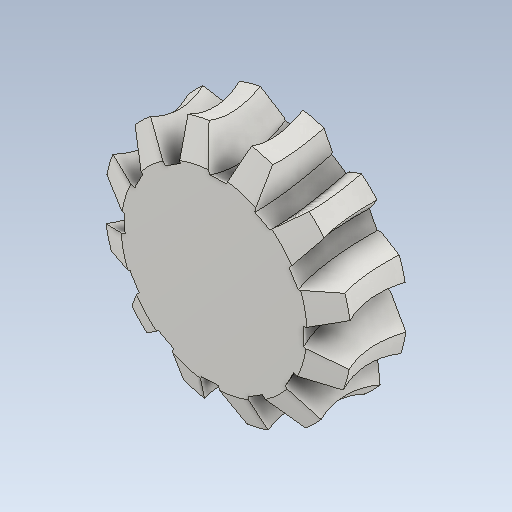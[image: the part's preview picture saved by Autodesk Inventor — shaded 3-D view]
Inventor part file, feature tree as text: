
AUTODESK INVENTOR PART (.ipt)
format: ipt  version: 2021 (Build 250183000, 183)  size: 324,096 bytes
history: native  units: mm (DEFAULTED — no unit token found)
features: other x8, plane x3, pattern_circular x1, sketch x1
ambient origin geometry x5: Origin, X Axis, Y Axis, Z Axis, Center Point
bodies: Solid1 (feature_tree)
feature tree (13):
  other  "Tooth Plane"
  other  "Base Body Sketch"
  other  "Base Body"
  other  "Base Body2"
  plane  "Work Plane13"
  other  "Tooth"
  pattern_circular  "Tooth Pattern"  [2 undecoded]
  plane  "Work Plane14"
  plane  "Work Plane15"
  other  "Tooth Sketch"
  sketch  "Sketch8"  dims[d35=90.0deg d37=-0.996687mm d38=44.0mm d39=3.490659mm d40=15.2mm d41=20.0mm d42=3.769911mm d43=90.0deg d44=120.0mm d46=360.0deg d50=4.297754mm d68=44.0mm d69=0.0mm d73=0.0mm d75=15.0deg d77=48.0mm d78=20.0mm d79=0.0mm d80=0.0mm d81=0.0mm d82=0.0mm d83=15.0deg d84=0.0mm d85=180.0deg d86=44.0mm d87=60.0mm d89=32.0mm d90=90.0deg d92=20.0mm d93=44.0mm]
  other  "Srf1"
  other  "Pitch Diameter"
note: 2 required parameter values undecoded (feature->parameter linkage not recoverable at this tier; creation-order binding heuristic only, values carry confidence <= 0.55)
